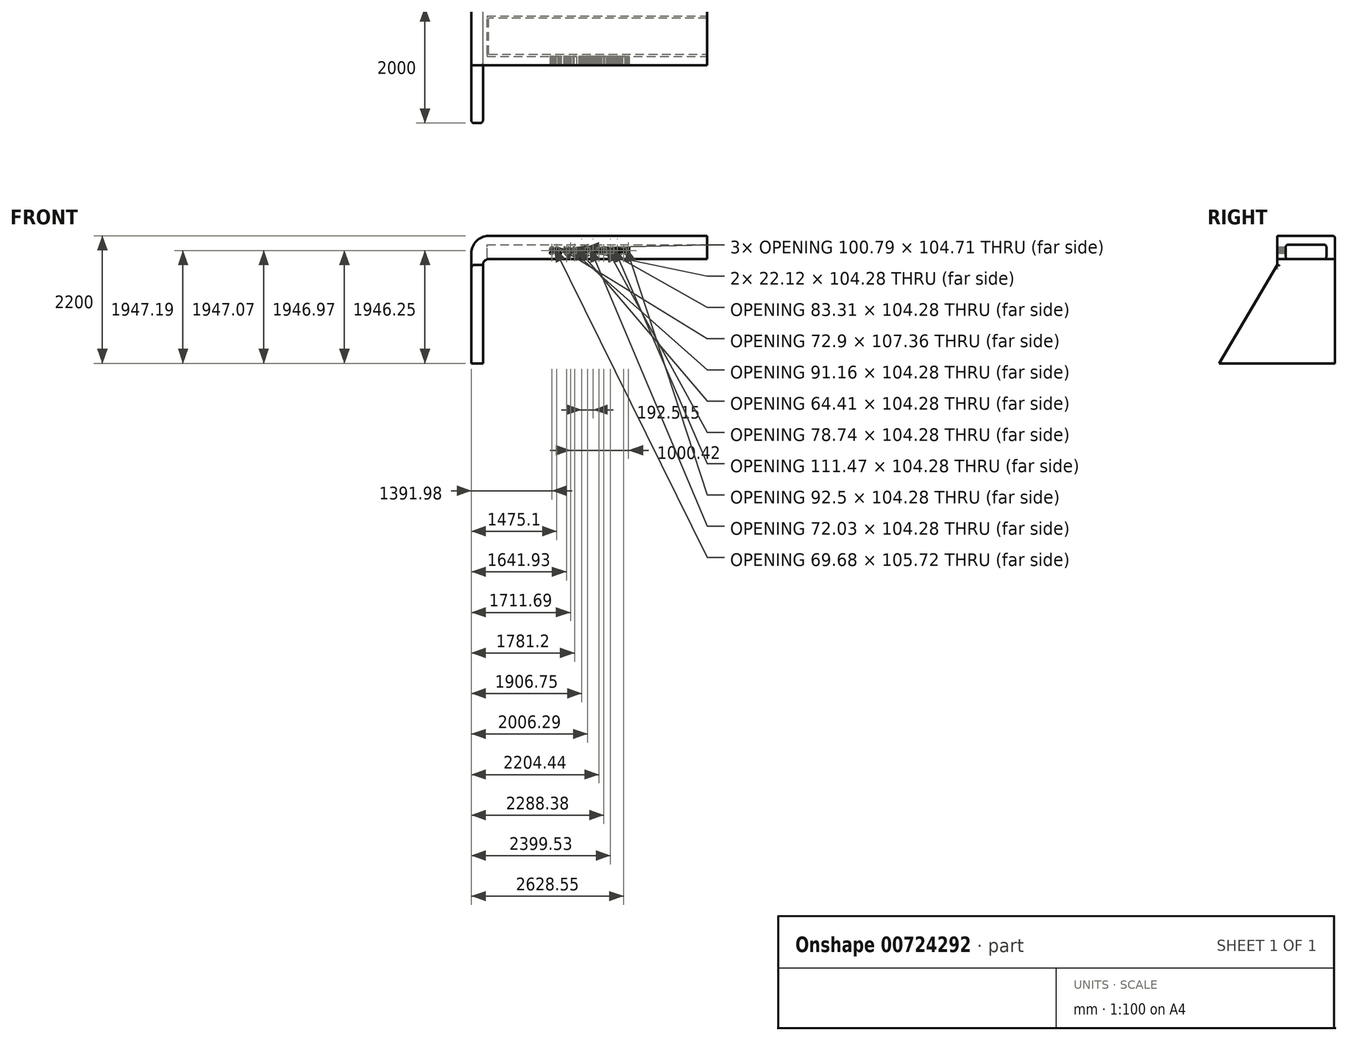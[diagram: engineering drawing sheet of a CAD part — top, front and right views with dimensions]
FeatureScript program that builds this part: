
annotation { "Feature Type Name" : "Feature", "Feature Type Description" : "" }
export const myFeature = defineFeature(function(context is Context, id is Id, definition is map)
    precondition{}
    {
        {
            var Q0;
            Q0=qCreatedBy(makeId("Front.planeOp"),FACE);
            var sketch = newSketch(context, id + "F0", { "sketchPlane" : qUnion([Q0])});
            skLineSegment(sketch, "E0.top", {"start": v(0, 2200) * mm, "end": v(-3769.7, 2200) * mm});
            skLineSegment(sketch, "E0.left", {"start": v(0, 1800) * mm, "end": v(0, 2200) * mm});
            skLineSegment(sketch, "E0.right", {"start": v(-3869.7, 0) * mm, "end": v(-3869.7, 1800) * mm});
            skLineSegment(sketch, "E1.top", {"start": v(-3869.7, 0) * mm, "end": v(-4069.7, 0) * mm});
            skLineSegment(sketch, "E1.left", {"start": v(-3869.7, 1700) * mm, "end": v(-3869.7, 0) * mm});
            skLineSegment(sketch, "E1.right", {"start": v(-4069.7, 1900) * mm, "end": v(-4069.7, 0) * mm});
            skLineSegment(sketch, "E2.bottom", {"start": v(-3769.7, 2200) * mm, "end": v(0, 2200) * mm});
            skLineSegment(sketch, "E2.top", {"start": v(-3769.7, 1800) * mm, "end": v(0, 1800) * mm});
            skLineSegment(sketch, "E2.right", {"start": v(0, 2200) * mm, "end": v(0, 1800) * mm});
            skPoint(sketch, "E3.visualSharp", {"position": v(-3869.7, 1800) * mm});
            skArc(sketch, "E3.filletArc", {"start": v(-3769.7, 1800) * mm, "mid": v(-3840.41, 1770.71) * mm, "end": v(-3869.7, 1700) * mm});
            skLineSegment(sketch, "E4", {"start": v(-3769.7, 1800) * mm, "end": v(-3769.7, 2265.31) * mm, "construction": true});
            skLineSegment(sketch, "E5", {"start": v(-4150.98, 1900) * mm, "end": v(-3536.97, 1900) * mm, "construction": true});
            skArc(sketch, "E6", {"start": v(-4069.7, 1900) * mm, "mid": v(-3981.83, 2112.13) * mm, "end": v(-3769.7, 2200) * mm});
            skSolve(sketch);
        }
        {
            var Q0;
            Q0=makeQuery(id+"F0.imprint","IMPRINT",FACE,{"disambiguationData":[TD([[makeQuery(id+"F0.imprint","IMPRINT",EDGE,{"derivedFrom":sQuery(id+"F0.wireOp",EDGE,"E0.top")}),1.0]])]});
            extrude(context, id + "F1", {"entities" : qUnion([Q0]), "depth" : 1000 * mm, "offsetDistance" : 25 * mm});
        }
        {
            var Q0;
            Q0=makeQuery(id+"F1.opExtrude","SWEPT_FACE",FACE,{"disambiguationData":[OSD([sQuery(id+"F0.wireOp",EDGE,"E0.left")])]});
            var sketch = newSketch(context, id + "F2", { "sketchPlane" : qUnion([Q0])});
            skLineSegment(sketch, "E7.bottom", {"start": v(-850, 1800) * mm, "end": v(-150, 1800) * mm});
            skLineSegment(sketch, "E7.top", {"start": v(-850, 2050) * mm, "end": v(-150, 2050) * mm});
            skLineSegment(sketch, "E7.left", {"start": v(-850, 1800) * mm, "end": v(-850, 2050) * mm});
            skLineSegment(sketch, "E7.right", {"start": v(-150, 1800) * mm, "end": v(-150, 2050) * mm});
            skSolve(sketch);
        }
        {
            var Q0;
            Q0 = qSketchRegion(id + "F2", true);
            extrude(context, id + "F3", {"entities" : qUnion([Q0]), "operationType" : NewBodyOperationType.REMOVE, "oppositeDirection" : true, "depth" : 3800 * mm, "offsetDistance" : 25 * mm});
        }
        {
            var Q0;
            Q0=makeQuery(id+"F1.opExtrude","SWEPT_FACE",FACE,{"disambiguationData":[OSD([sQuery(id+"F0.wireOp",EDGE,"E1.right")])]});
            var sketch = newSketch(context, id + "F4", { "sketchPlane" : qUnion([Q0])});
            skLineSegment(sketch, "E8.0", {"start": v(1000, 1700) * mm, "end": v(1000, 0) * mm});
            skLineSegment(sketch, "E9.0", {"start": v(1000, 0) * mm, "end": v(0, 0) * mm});
            skLineSegment(sketch, "E10.top", {"start": v(1000, 0) * mm, "end": v(2000, 0) * mm});
            skLineSegment(sketch, "E10.left", {"start": v(1000, 1900) * mm, "end": v(1000, 0) * mm});
            skLineSegment(sketch, "E11", {"start": v(2000, 0) * mm, "end": v(1000, 1700) * mm});
            skPoint(sketch, "E12.0.end.orphan", {"position": v(0, 1900) * mm});
            skSolve(sketch);
        }
        {
            var Q0;
            Q0 = qSketchRegion(id + "F4", true);
            extrude(context, id + "F5", {"entities" : qUnion([Q0]), "operationType" : NewBodyOperationType.ADD, "oppositeDirection" : true, "depth" : 200 * mm, "offsetDistance" : 25 * mm});
        }
        {
            var Q0;
            Q0=makeQuery(id+"F5.opExtrude","CAP_EDGE",EDGE,{"disambiguationData":[OSD([sQuery(id+"F4.wireOp",EDGE,"E11")])],"isStart":false});
            var Q1;
            Q1=makeQuery(id+"F5.opExtrude","CAP_EDGE",EDGE,{"disambiguationData":[OSD([sQuery(id+"F4.wireOp",EDGE,"E11")])],"isStart":true});
            var Q2;
            Q2=makeQuery(id+"F1.opExtrude","CAP_EDGE",EDGE,{"disambiguationData":[OSD([sQuery(id+"F0.wireOp",EDGE,"E0.right")])],"isStart":true});
            var Q3;
            Q3=makeQuery(id+"F1.opExtrude","CAP_EDGE",EDGE,{"disambiguationData":[OSD([sQuery(id+"F0.wireOp",EDGE,"E2.top")])],"isStart":false});
            var Q4;
            Q4=makeQuery(id+"F5.opExtrude","SWEPT_EDGE",EDGE,{"disambiguationData":[OSD([sQuery(id+"F4.wireOp",EDGE,"E10.left"),sQuery(id+"F4.wireOp",EDGE,"E11")])]});
            var Q5;
            Q5=makeQuery(id+"F1.opExtrude","CAP_EDGE",EDGE,{"disambiguationData":[OSD([sQuery(id+"F0.wireOp",EDGE,"E1.right")])],"isStart":true});
            var Q6;
            Q6=makeQuery(id+"F1.opExtrude","CAP_EDGE",EDGE,{"disambiguationData":[OSD([sQuery(id+"F0.wireOp",EDGE,"E3.filletArc")])],"isStart":true});
            var Q7;
            {var subQ0=sQuery(id+"F0.wireOp",EDGE,"E2.top");var subQ1=sQuery(id+"F2.wireOp",EDGE,"E7.left");Q7=makeQuery(id+"F3.boolean.opBoolean","COPY",EDGE,{"disambiguationData":[topologyDisambiguationEdgeConnected([makeQuery(id+"F1.opExtrude","SWEPT_FACE",FACE,{"disambiguationData":[OSD([subQ0])]})])],"derivedFrom":makeQuery(id+"F3.opExtrude","SWEPT_EDGE",EDGE,{"disambiguationData":[OSD([sQuery(id+"F0.wireOp",EDGE,"E0.left"),subQ0,sQuery(id+"F2.wireOp",EDGE,"E7.bottom"),subQ1])]})});}
            var Q8;
            {var subQ0=sQuery(id+"F0.wireOp",EDGE,"E2.top");var subQ1=sQuery(id+"F2.wireOp",EDGE,"E7.right");Q8=makeQuery(id+"F3.boolean.opBoolean","COPY",EDGE,{"disambiguationData":[topologyDisambiguationEdgeConnected([makeQuery(id+"F1.opExtrude","SWEPT_FACE",FACE,{"disambiguationData":[OSD([subQ0])]})])],"derivedFrom":makeQuery(id+"F3.opExtrude","SWEPT_EDGE",EDGE,{"disambiguationData":[OSD([sQuery(id+"F0.wireOp",EDGE,"E0.left"),subQ0,sQuery(id+"F2.wireOp",EDGE,"E7.bottom"),subQ1])]})});}
            var Q9;
            Q9=makeQuery(id+"F3.boolean.opBoolean","COPY",EDGE,{"derivedFrom":makeQuery(id+"F3.opExtrude","SWEPT_EDGE",EDGE,{"disambiguationData":[OSD([sQuery(id+"F2.wireOp",EDGE,"E7.top"),sQuery(id+"F2.wireOp",EDGE,"E7.left")])]})});
            var Q10;
            Q10=makeQuery(id+"F3.boolean.opBoolean","COPY",EDGE,{"derivedFrom":makeQuery(id+"F3.opExtrude","SWEPT_EDGE",EDGE,{"disambiguationData":[OSD([sQuery(id+"F2.wireOp",EDGE,"E7.top"),sQuery(id+"F2.wireOp",EDGE,"E7.right")])]})});
            fillet(context, id + "F6", {"entities" : qUnion([Q0, Q1, Q2, Q3, Q4, Q5, Q6, Q7, Q8, Q9, Q10]), "radius" : 40 * mm, "tangentPropagation" : true, "allowEdgeOverflow" : false});
        }
        {
            var Q0;
            Q0=makeQuery(id+"F1.opExtrude","CAP_FACE",FACE,{"disambiguationData":[OSD([sQuery(id+"F0.wireOp",EDGE,"E0.top"),sQuery(id+"F0.wireOp",EDGE,"E0.left"),sQuery(id+"F0.wireOp",EDGE,"E0.right"),sQuery(id+"F0.wireOp",EDGE,"E1.top"),sQuery(id+"F0.wireOp",EDGE,"E1.right"),sQuery(id+"F0.wireOp",EDGE,"E2.top"),sQuery(id+"F0.wireOp",EDGE,"E3.filletArc"),sQuery(id+"F0.wireOp",EDGE,"E6")])],"isStart":false});
            var sketch = newSketch(context, id + "F7", { "sketchPlane" : qUnion([Q0])});
            skText(sketch, "E13", { "text": "50. YIL APARTMANI", "fontName": "OpenSans-Bold.ttf"});
            const initialGuessF7  = {"E13": [-2.7197, 1.89483, 1, 0, 0.10517]};
            skSetInitialGuess(sketch, initialGuessF7);
            skSolve(sketch);
        }
        {
            var Q0;
            Q0 = qSketchRegion(id + "F7", true);
            extrude(context, id + "F8", {"entities" : qUnion([Q0]), "operationType" : NewBodyOperationType.REMOVE, "oppositeDirection" : true, "depth" : 200 * mm, "offsetDistance" : 25 * mm});
        }
    });
